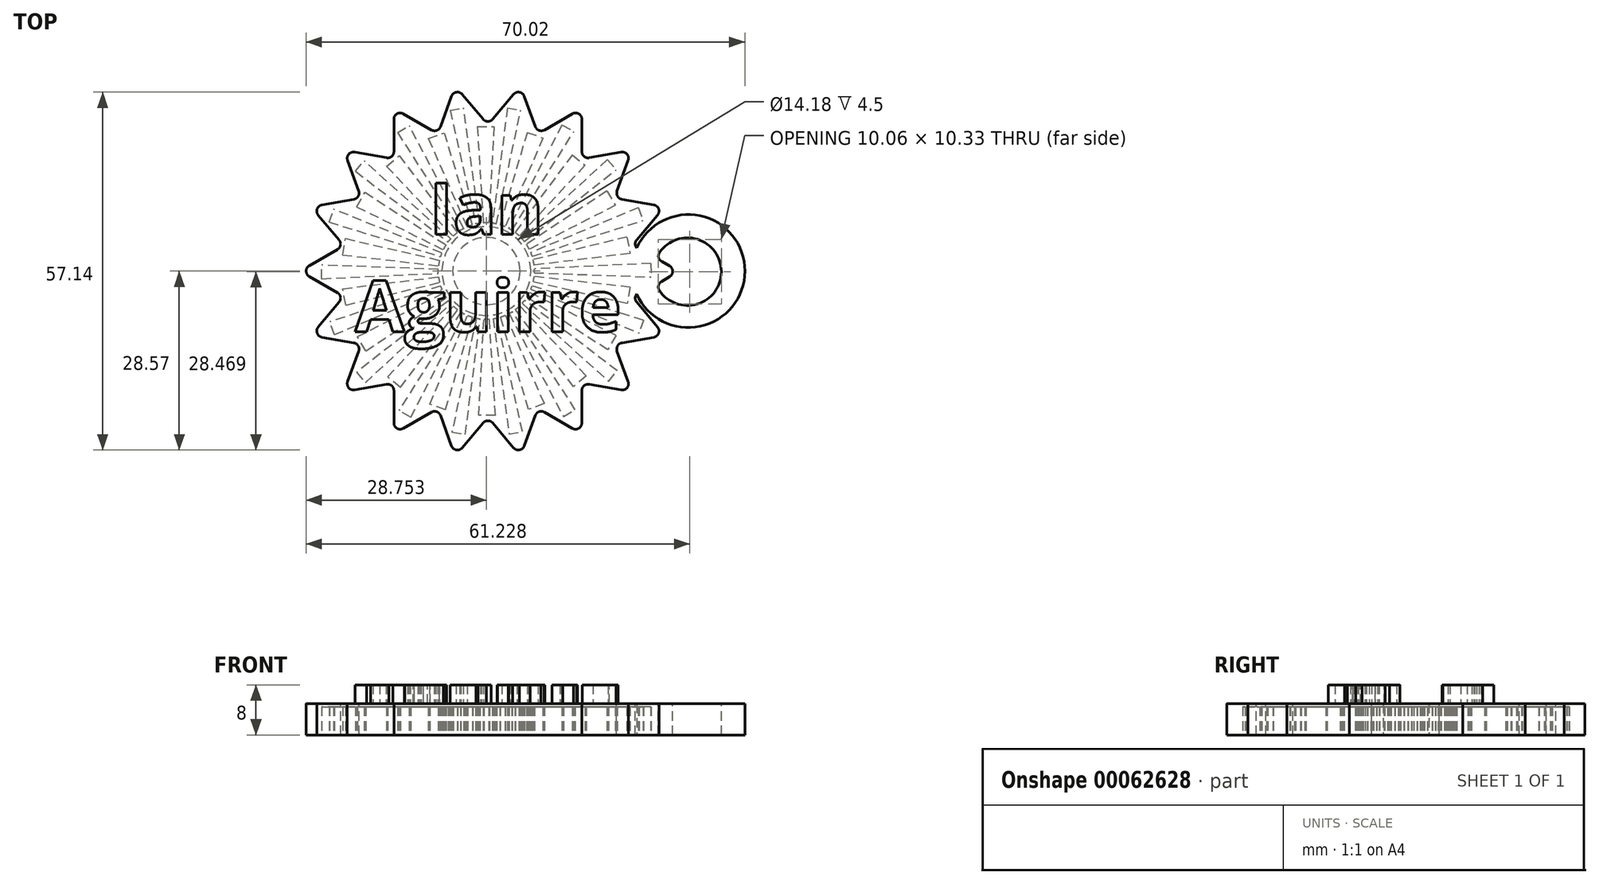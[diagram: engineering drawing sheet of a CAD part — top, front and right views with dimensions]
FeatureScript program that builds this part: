
annotation { "Feature Type Name" : "Feature", "Feature Type Description" : "" }
export const myFeature = defineFeature(function(context is Context, id is Id, definition is map)
    precondition{}
    {
        {
            var Q0;
            Q0=qCreatedBy(makeId("Top.planeOp"),FACE);
            var sketch = newSketch(context, id + "F0", { "sketchPlane" : qUnion([Q0])});
            skLineSegment(sketch, "E0", {"start": v(-64.22, 4.05) * mm, "end": v(-69.43, 10.26) * mm});
            skLineSegment(sketch, "E1", {"start": v(-69.43, 10.26) * mm, "end": v(-61.45, 11.67) * mm});
            skCircle(sketch, "E2.0", {"center": v(-41.24, 0) * mm, "radius": 30 * mm, "construction": true});
            skLineSegment(sketch, "E3", {"start": v(-61.45, 11.67) * mm, "end": v(-64.22, 19.28) * mm});
            skLineSegment(sketch, "E4", {"start": v(-64.22, 19.28) * mm, "end": v(-56.24, 17.88) * mm});
            skLineSegment(sketch, "E5", {"start": v(-56.24, 17.88) * mm, "end": v(-56.24, 25.98) * mm});
            skLineSegment(sketch, "E6", {"start": v(-56.24, 25.98) * mm, "end": v(-49.22, 21.93) * mm});
            skLineSegment(sketch, "E7", {"start": v(-49.22, 21.93) * mm, "end": v(-46.45, 29.54) * mm});
            skLineSegment(sketch, "E8", {"start": v(-46.45, 29.54) * mm, "end": v(-41.24, 23.34) * mm});
            skLineSegment(sketch, "E9", {"start": v(-41.24, 23.34) * mm, "end": v(-36.03, 29.54) * mm});
            skLineSegment(sketch, "E10", {"start": v(-36.03, 29.54) * mm, "end": v(-33.26, 21.93) * mm});
            skLineSegment(sketch, "E11", {"start": v(-33.26, 21.93) * mm, "end": v(-26.24, 25.98) * mm});
            skLineSegment(sketch, "E12", {"start": v(-26.24, 25.98) * mm, "end": v(-26.24, 17.88) * mm});
            skLineSegment(sketch, "E13", {"start": v(-26.24, 17.88) * mm, "end": v(-18.26, 19.28) * mm});
            skLineSegment(sketch, "E14", {"start": v(-18.26, 19.28) * mm, "end": v(-21.03, 11.67) * mm});
            skLineSegment(sketch, "E15", {"start": v(-21.03, 11.67) * mm, "end": v(-13.05, 10.26) * mm});
            skLineSegment(sketch, "E16", {"start": v(-13.05, 10.26) * mm, "end": v(-18.26, 4.05) * mm});
            skLineSegment(sketch, "E17", {"start": v(-18.26, 4.05) * mm, "end": v(-11.24, 0) * mm});
            skLineSegment(sketch, "E18", {"start": v(-11.24, 0) * mm, "end": v(-18.26, -4.05) * mm});
            skLineSegment(sketch, "E19", {"start": v(-18.26, -4.05) * mm, "end": v(-13.05, -10.26) * mm});
            skLineSegment(sketch, "E20", {"start": v(-13.05, -10.26) * mm, "end": v(-21.03, -11.67) * mm});
            skLineSegment(sketch, "E21", {"start": v(-21.03, -11.67) * mm, "end": v(-18.26, -19.28) * mm});
            skLineSegment(sketch, "E22", {"start": v(-18.26, -19.28) * mm, "end": v(-26.24, -17.88) * mm});
            skLineSegment(sketch, "E23", {"start": v(-26.24, -17.88) * mm, "end": v(-26.24, -25.98) * mm});
            skLineSegment(sketch, "E24", {"start": v(-26.24, -25.98) * mm, "end": v(-33.26, -21.93) * mm});
            skLineSegment(sketch, "E25", {"start": v(-33.26, -21.93) * mm, "end": v(-36.03, -29.54) * mm});
            skLineSegment(sketch, "E26", {"start": v(-46.45, -29.54) * mm, "end": v(-49.22, -21.93) * mm});
            skLineSegment(sketch, "E27", {"start": v(-49.22, -21.93) * mm, "end": v(-56.24, -25.98) * mm});
            skLineSegment(sketch, "E28", {"start": v(-56.24, -25.98) * mm, "end": v(-56.24, -17.88) * mm});
            skLineSegment(sketch, "E29", {"start": v(-56.24, -17.88) * mm, "end": v(-64.22, -19.28) * mm});
            skLineSegment(sketch, "E30", {"start": v(-64.22, -19.28) * mm, "end": v(-61.45, -11.67) * mm});
            skLineSegment(sketch, "E31", {"start": v(-61.45, -11.67) * mm, "end": v(-69.43, -10.26) * mm});
            skLineSegment(sketch, "E32", {"start": v(-69.43, -10.26) * mm, "end": v(-64.22, -4.05) * mm});
            skLineSegment(sketch, "E33", {"start": v(-64.22, -4.05) * mm, "end": v(-71.24, 0) * mm});
            skLineSegment(sketch, "E34", {"start": v(-71.24, 0) * mm, "end": v(-64.22, 4.05) * mm});
            skLineSegment(sketch, "E35", {"start": v(-46.45, -29.54) * mm, "end": v(-41.24, -23.34) * mm});
            skLineSegment(sketch, "E36", {"start": v(-41.24, -23.34) * mm, "end": v(-36.03, -29.54) * mm});
            skSolve(sketch);
        }
        {
            var Q0;
            Q0=qSketchRegion(id+"F0",true);
            extrude(context, id + "F1", {"entities" : qUnion([Q0]), "depth" : 5 * mm});
        }
        {
            var Q0;
            Q0=makeQuery(id+"F1.opExtrude","SWEPT_EDGE",EDGE,{"disambiguationData":[OSD([sQuery(id+"F0.wireOp",EDGE,"E26"),sQuery(id+"F0.wireOp",EDGE,"E27")])]});
            var Q1;
            Q1=makeQuery(id+"F1.opExtrude","SWEPT_EDGE",EDGE,{"disambiguationData":[OSD([sQuery(id+"F0.wireOp",EDGE,"E28"),sQuery(id+"F0.wireOp",EDGE,"E29")])]});
            var Q2;
            Q2=makeQuery(id+"F1.opExtrude","SWEPT_EDGE",EDGE,{"disambiguationData":[OSD([sQuery(id+"F0.wireOp",EDGE,"E30"),sQuery(id+"F0.wireOp",EDGE,"E31")])]});
            var Q3;
            Q3=makeQuery(id+"F1.opExtrude","SWEPT_EDGE",EDGE,{"disambiguationData":[OSD([sQuery(id+"F0.wireOp",EDGE,"E32"),sQuery(id+"F0.wireOp",EDGE,"E33")])]});
            var Q4;
            Q4=makeQuery(id+"F1.opExtrude","SWEPT_EDGE",EDGE,{"disambiguationData":[OSD([sQuery(id+"F0.wireOp",EDGE,"E0"),sQuery(id+"F0.wireOp",EDGE,"E34")])]});
            var Q5;
            Q5=makeQuery(id+"F1.opExtrude","SWEPT_EDGE",EDGE,{"disambiguationData":[OSD([sQuery(id+"F0.wireOp",EDGE,"E1"),sQuery(id+"F0.wireOp",EDGE,"E3")])]});
            var Q6;
            Q6=makeQuery(id+"F1.opExtrude","SWEPT_EDGE",EDGE,{"disambiguationData":[OSD([sQuery(id+"F0.wireOp",EDGE,"E4"),sQuery(id+"F0.wireOp",EDGE,"E5")])]});
            var Q7;
            Q7=makeQuery(id+"F1.opExtrude","SWEPT_EDGE",EDGE,{"disambiguationData":[OSD([sQuery(id+"F0.wireOp",EDGE,"E6"),sQuery(id+"F0.wireOp",EDGE,"E7")])]});
            var Q8;
            Q8=makeQuery(id+"F1.opExtrude","SWEPT_EDGE",EDGE,{"disambiguationData":[OSD([sQuery(id+"F0.wireOp",EDGE,"E8"),sQuery(id+"F0.wireOp",EDGE,"E9")])]});
            var Q9;
            Q9=makeQuery(id+"F1.opExtrude","SWEPT_EDGE",EDGE,{"disambiguationData":[OSD([sQuery(id+"F0.wireOp",EDGE,"E10"),sQuery(id+"F0.wireOp",EDGE,"E11")])]});
            var Q10;
            Q10=makeQuery(id+"F1.opExtrude","SWEPT_EDGE",EDGE,{"disambiguationData":[OSD([sQuery(id+"F0.wireOp",EDGE,"E35"),sQuery(id+"F0.wireOp",EDGE,"E36")])]});
            var Q11;
            Q11=makeQuery(id+"F1.opExtrude","SWEPT_EDGE",EDGE,{"disambiguationData":[OSD([sQuery(id+"F0.wireOp",EDGE,"E24"),sQuery(id+"F0.wireOp",EDGE,"E25")])]});
            var Q12;
            Q12=makeQuery(id+"F1.opExtrude","SWEPT_EDGE",EDGE,{"disambiguationData":[OSD([sQuery(id+"F0.wireOp",EDGE,"E22"),sQuery(id+"F0.wireOp",EDGE,"E23")])]});
            var Q13;
            Q13=makeQuery(id+"F1.opExtrude","SWEPT_EDGE",EDGE,{"disambiguationData":[OSD([sQuery(id+"F0.wireOp",EDGE,"E20"),sQuery(id+"F0.wireOp",EDGE,"E21")])]});
            var Q14;
            Q14=makeQuery(id+"F1.opExtrude","SWEPT_EDGE",EDGE,{"disambiguationData":[OSD([sQuery(id+"F0.wireOp",EDGE,"E12"),sQuery(id+"F0.wireOp",EDGE,"E13")])]});
            var Q15;
            Q15=makeQuery(id+"F1.opExtrude","SWEPT_EDGE",EDGE,{"disambiguationData":[OSD([sQuery(id+"F0.wireOp",EDGE,"E14"),sQuery(id+"F0.wireOp",EDGE,"E15")])]});
            var Q16;
            Q16=makeQuery(id+"F1.opExtrude","SWEPT_EDGE",EDGE,{"disambiguationData":[OSD([sQuery(id+"F0.wireOp",EDGE,"E16"),sQuery(id+"F0.wireOp",EDGE,"E17")])]});
            var Q17;
            Q17=makeQuery(id+"F1.opExtrude","SWEPT_EDGE",EDGE,{"disambiguationData":[OSD([sQuery(id+"F0.wireOp",EDGE,"E18"),sQuery(id+"F0.wireOp",EDGE,"E19")])]});
            fillet(context, id + "F2", {"entities" : qUnion([Q0, Q1, Q2, Q3, Q4, Q5, Q6, Q7, Q8, Q9, Q10, Q11, Q12, Q13, Q14, Q15, Q16, Q17]), "radius" : 1 * mm, "tangentPropagation" : true, "allowEdgeOverflow" : false});
        }
        {
            var Q0;
            Q0=makeQuery(id+"F1.opExtrude","SWEPT_EDGE",EDGE,{"disambiguationData":[OSD([sQuery(id+"F0.wireOp",EDGE,"E9"),sQuery(id+"F0.wireOp",EDGE,"E10")])]});
            var Q1;
            Q1=makeQuery(id+"F1.opExtrude","SWEPT_EDGE",EDGE,{"disambiguationData":[OSD([sQuery(id+"F0.wireOp",EDGE,"E11"),sQuery(id+"F0.wireOp",EDGE,"E12")])]});
            var Q2;
            Q2=makeQuery(id+"F1.opExtrude","SWEPT_EDGE",EDGE,{"disambiguationData":[OSD([sQuery(id+"F0.wireOp",EDGE,"E13"),sQuery(id+"F0.wireOp",EDGE,"E14")])]});
            var Q3;
            Q3=makeQuery(id+"F1.opExtrude","SWEPT_EDGE",EDGE,{"disambiguationData":[OSD([sQuery(id+"F0.wireOp",EDGE,"E15"),sQuery(id+"F0.wireOp",EDGE,"E16")])]});
            var Q4;
            Q4=makeQuery(id+"F1.opExtrude","SWEPT_EDGE",EDGE,{"disambiguationData":[OSD([sQuery(id+"F0.wireOp",EDGE,"E17"),sQuery(id+"F0.wireOp",EDGE,"E18")])]});
            var Q5;
            Q5=makeQuery(id+"F1.opExtrude","SWEPT_EDGE",EDGE,{"disambiguationData":[OSD([sQuery(id+"F0.wireOp",EDGE,"E19"),sQuery(id+"F0.wireOp",EDGE,"E20")])]});
            var Q6;
            Q6=makeQuery(id+"F1.opExtrude","SWEPT_EDGE",EDGE,{"disambiguationData":[OSD([sQuery(id+"F0.wireOp",EDGE,"E5"),sQuery(id+"F0.wireOp",EDGE,"E6")])]});
            var Q7;
            Q7=makeQuery(id+"F1.opExtrude","SWEPT_EDGE",EDGE,{"disambiguationData":[OSD([sQuery(id+"F0.wireOp",EDGE,"E7"),sQuery(id+"F0.wireOp",EDGE,"E8")])]});
            var Q8;
            Q8=makeQuery(id+"F1.opExtrude","SWEPT_EDGE",EDGE,{"disambiguationData":[OSD([sQuery(id+"F0.wireOp",EDGE,"E3"),sQuery(id+"F0.wireOp",EDGE,"E4")])]});
            var Q9;
            Q9=makeQuery(id+"F1.opExtrude","SWEPT_EDGE",EDGE,{"disambiguationData":[OSD([sQuery(id+"F0.wireOp",EDGE,"E0"),sQuery(id+"F0.wireOp",EDGE,"E1")])]});
            var Q10;
            Q10=makeQuery(id+"F1.opExtrude","SWEPT_EDGE",EDGE,{"disambiguationData":[OSD([sQuery(id+"F0.wireOp",EDGE,"E33"),sQuery(id+"F0.wireOp",EDGE,"E34")])]});
            var Q11;
            Q11=makeQuery(id+"F1.opExtrude","SWEPT_EDGE",EDGE,{"disambiguationData":[OSD([sQuery(id+"F0.wireOp",EDGE,"E31"),sQuery(id+"F0.wireOp",EDGE,"E32")])]});
            var Q12;
            Q12=makeQuery(id+"F1.opExtrude","SWEPT_EDGE",EDGE,{"disambiguationData":[OSD([sQuery(id+"F0.wireOp",EDGE,"E29"),sQuery(id+"F0.wireOp",EDGE,"E30")])]});
            var Q13;
            Q13=makeQuery(id+"F1.opExtrude","SWEPT_EDGE",EDGE,{"disambiguationData":[OSD([sQuery(id+"F0.wireOp",EDGE,"E27"),sQuery(id+"F0.wireOp",EDGE,"E28")])]});
            var Q14;
            Q14=makeQuery(id+"F1.opExtrude","SWEPT_EDGE",EDGE,{"disambiguationData":[OSD([sQuery(id+"F0.wireOp",EDGE,"E26"),sQuery(id+"F0.wireOp",EDGE,"E35")])]});
            var Q15;
            Q15=makeQuery(id+"F1.opExtrude","SWEPT_EDGE",EDGE,{"disambiguationData":[OSD([sQuery(id+"F0.wireOp",EDGE,"E25"),sQuery(id+"F0.wireOp",EDGE,"E36")])]});
            var Q16;
            Q16=makeQuery(id+"F1.opExtrude","SWEPT_EDGE",EDGE,{"disambiguationData":[OSD([sQuery(id+"F0.wireOp",EDGE,"E23"),sQuery(id+"F0.wireOp",EDGE,"E24")])]});
            var Q17;
            Q17=makeQuery(id+"F1.opExtrude","SWEPT_EDGE",EDGE,{"disambiguationData":[OSD([sQuery(id+"F0.wireOp",EDGE,"E21"),sQuery(id+"F0.wireOp",EDGE,"E22")])]});
            fillet(context, id + "F3", {"entities" : qUnion([Q0, Q1, Q2, Q3, Q4, Q5, Q6, Q7, Q8, Q9, Q10, Q11, Q12, Q13, Q14, Q15, Q16, Q17]), "radius" : 1 * mm, "tangentPropagation" : true, "allowEdgeOverflow" : false});
        }
        {
            var Q0;
            Q0=qCreatedBy(makeId("Top.planeOp"),FACE);
            var sketch = newSketch(context, id + "F4", { "sketchPlane" : qUnion([Q0])});
            skCircle(sketch, "E37", {"center": v(-9.24, 0) * mm, "radius": 9.02 * mm});
            skSolve(sketch);
        }
        {
            var Q0;
            Q0=qSketchRegion(id+"F4",true);
            var Q1;
            {var subQ0=sQuery(id+"F0.wireOp",EDGE,"E30");var subQ1=sQuery(id+"F0.wireOp",EDGE,"E16");var subQ2=sQuery(id+"F0.wireOp",EDGE,"E31");var subQ3=sQuery(id+"F0.wireOp",EDGE,"E27");var subQ4=sQuery(id+"F0.wireOp",EDGE,"E23");var subQ5=sQuery(id+"F0.wireOp",EDGE,"E21");var subQ6=sQuery(id+"F0.wireOp",EDGE,"E13");var subQ7=sQuery(id+"F0.wireOp",EDGE,"E14");var subQ8=sQuery(id+"F0.wireOp",EDGE,"E20");var subQ9=sQuery(id+"F0.wireOp",EDGE,"E22");var subQ10=sQuery(id+"F0.wireOp",EDGE,"E19");var subQ11=sQuery(id+"F0.wireOp",EDGE,"E11");var subQ12=sQuery(id+"F0.wireOp",EDGE,"E18");var subQ13=sQuery(id+"F0.wireOp",EDGE,"E17");var subQ14=sQuery(id+"F0.wireOp",EDGE,"E12");var subQ15=sQuery(id+"F0.wireOp",EDGE,"E4");var subQ16=sQuery(id+"F0.wireOp",EDGE,"E3");var subQ17=sQuery(id+"F0.wireOp",EDGE,"E32");var subQ18=sQuery(id+"F0.wireOp",EDGE,"E1");var subQ19=sQuery(id+"F0.wireOp",EDGE,"E9");var subQ20=sQuery(id+"F0.wireOp",EDGE,"E0");var subQ21=sQuery(id+"F0.wireOp",EDGE,"E5");var subQ22=sQuery(id+"F0.wireOp",EDGE,"E6");var subQ23=sQuery(id+"F0.wireOp",EDGE,"E7");var subQ24=sQuery(id+"F0.wireOp",EDGE,"E36");var subQ25=sQuery(id+"F0.wireOp",EDGE,"E15");var subQ26=sQuery(id+"F0.wireOp",EDGE,"E8");var subQ27=sQuery(id+"F0.wireOp",EDGE,"E34");var subQ28=sQuery(id+"F0.wireOp",EDGE,"E25");var subQ29=sQuery(id+"F0.wireOp",EDGE,"E29");var subQ30=sQuery(id+"F0.wireOp",EDGE,"E26");var subQ31=sQuery(id+"F0.wireOp",EDGE,"E35");var subQ32=sQuery(id+"F0.wireOp",EDGE,"E33");var subQ33=sQuery(id+"F0.wireOp",EDGE,"E24");var subQ34=sQuery(id+"F0.wireOp",EDGE,"E10");var subQ35=sQuery(id+"F0.wireOp",EDGE,"E28");Q1=makeQuery(id+"FIdaEZY0NoQjCEp_1.boolean.opBoolean","SPLIT",FACE,{"disambiguationData":[TD([makeQuery(id+"F1.opExtrude","SWEPT_FACE",FACE,{"disambiguationData":[OSD([subQ20])]})])],"derivedFrom":makeQuery(id+"F1.opExtrude","CAP_FACE",FACE,{"disambiguationData":[OSD([subQ20,subQ18,subQ16,subQ15,subQ21,subQ22,subQ23,subQ26,subQ19,subQ34,subQ11,subQ14,subQ6,subQ7,subQ25,subQ1,subQ13,subQ12,subQ10,subQ8,subQ5,subQ9,subQ4,subQ33,subQ28,subQ30,subQ3,subQ35,subQ29,subQ0,subQ2,subQ17,subQ32,subQ27,subQ31,subQ24])],"isStart":false})});}
            extrude(context, id + "F5", {"entities" : qUnion([Q0]), "operationType" : NewBodyOperationType.ADD, "endBound" : BoundingType.UP_TO_SURFACE, "endBoundEntityFace" : qUnion([Q1]), "depth" : 25 * mm});
        }
        {
            var Q0;
            {var subQ0=sQuery(id+"F0.wireOp",EDGE,"E36");var subQ1=sQuery(id+"F0.wireOp",EDGE,"E35");var subQ2=sQuery(id+"F0.wireOp",EDGE,"E34");var subQ3=sQuery(id+"F0.wireOp",EDGE,"E33");var subQ4=sQuery(id+"F0.wireOp",EDGE,"E32");var subQ5=sQuery(id+"F0.wireOp",EDGE,"E31");var subQ6=sQuery(id+"F0.wireOp",EDGE,"E30");var subQ7=sQuery(id+"F0.wireOp",EDGE,"E29");var subQ8=sQuery(id+"F0.wireOp",EDGE,"E28");var subQ9=sQuery(id+"F0.wireOp",EDGE,"E27");var subQ10=sQuery(id+"F0.wireOp",EDGE,"E26");var subQ11=sQuery(id+"F0.wireOp",EDGE,"E25");var subQ12=sQuery(id+"F0.wireOp",EDGE,"E24");var subQ13=sQuery(id+"F0.wireOp",EDGE,"E23");var subQ14=sQuery(id+"F0.wireOp",EDGE,"E22");var subQ15=sQuery(id+"F0.wireOp",EDGE,"E21");var subQ16=sQuery(id+"F0.wireOp",EDGE,"E20");var subQ17=sQuery(id+"F0.wireOp",EDGE,"E19");var subQ18=sQuery(id+"F0.wireOp",EDGE,"E18");var subQ19=sQuery(id+"F0.wireOp",EDGE,"E17");var subQ20=sQuery(id+"F0.wireOp",EDGE,"E16");var subQ21=sQuery(id+"F0.wireOp",EDGE,"E15");var subQ22=sQuery(id+"F0.wireOp",EDGE,"E14");var subQ23=sQuery(id+"F0.wireOp",EDGE,"E13");var subQ24=sQuery(id+"F0.wireOp",EDGE,"E12");var subQ25=sQuery(id+"F0.wireOp",EDGE,"E11");var subQ26=sQuery(id+"F0.wireOp",EDGE,"E10");var subQ27=sQuery(id+"F0.wireOp",EDGE,"E9");var subQ28=sQuery(id+"F0.wireOp",EDGE,"E8");var subQ29=sQuery(id+"F0.wireOp",EDGE,"E7");var subQ30=sQuery(id+"F0.wireOp",EDGE,"E6");var subQ31=sQuery(id+"F0.wireOp",EDGE,"E5");var subQ32=sQuery(id+"F0.wireOp",EDGE,"E4");var subQ33=sQuery(id+"F0.wireOp",EDGE,"E3");var subQ34=sQuery(id+"F0.wireOp",EDGE,"E1");var subQ35=sQuery(id+"F0.wireOp",EDGE,"E0");Q0=makeQuery(id+"F5.boolean.opBoolean","MERGE",FACE,{"derivedFrom":[makeQuery(id+"F1.opExtrude","CAP_FACE",FACE,{"disambiguationData":[OSD([subQ35,subQ34,subQ33,subQ32,subQ31,subQ30,subQ29,subQ28,subQ27,subQ26,subQ25,subQ24,subQ23,subQ22,subQ21,subQ20,subQ19,subQ18,subQ17,subQ16,subQ15,subQ14,subQ13,subQ12,subQ11,subQ10,subQ9,subQ8,subQ7,subQ6,subQ5,subQ4,subQ3,subQ2,subQ1,subQ0])],"isStart":false}),makeQuery(id+"F5.opExtrude","CAP_FACE",FACE,{"disambiguationData":[OSD([subQ35,subQ34,subQ33,subQ32,subQ31,subQ30,subQ29,subQ28,subQ27,subQ26,subQ25,subQ24,subQ23,subQ22,subQ21,subQ20,subQ19,subQ18,subQ17,subQ16,subQ15,subQ14,subQ13,subQ12,subQ11,subQ10,subQ9,subQ8,subQ7,subQ6,subQ5,subQ4,subQ3,subQ2,subQ1,subQ0])],"isStart":false})]});}
            var sketch = newSketch(context, id + "F6", { "sketchPlane" : qUnion([Q0])});
            skLineSegment(sketch, "E38", {"start": v(-14.37, 2) * mm, "end": v(-10.75, 0) * mm});
            skLineSegment(sketch, "E39", {"start": v(-10.75, 0) * mm, "end": v(-14.37, -2.19) * mm});
            skArc(sketch, "E40", {"start": v(-14.37, -2.19) * mm, "mid": v(-3.98, -0.1) * mm, "end": v(-14.37, 2) * mm});
            skSolve(sketch);
        }
        {
            var Q0;
            Q0=qSketchRegion(id+"F6",true);
            var Q1;
            Q1=makeQuery(id+"F5.boolean.opBoolean","MERGE",FACE,{"derivedFrom":[makeQuery(id+"F1.opExtrude","CAP_FACE",FACE,{"disambiguationData":[OSD([sQuery(id+"F0.wireOp",EDGE,"E0"),sQuery(id+"F0.wireOp",EDGE,"E1"),sQuery(id+"F0.wireOp",EDGE,"E3"),sQuery(id+"F0.wireOp",EDGE,"E4"),sQuery(id+"F0.wireOp",EDGE,"E5"),sQuery(id+"F0.wireOp",EDGE,"E6"),sQuery(id+"F0.wireOp",EDGE,"E7"),sQuery(id+"F0.wireOp",EDGE,"E8"),sQuery(id+"F0.wireOp",EDGE,"E9"),sQuery(id+"F0.wireOp",EDGE,"E10"),sQuery(id+"F0.wireOp",EDGE,"E11"),sQuery(id+"F0.wireOp",EDGE,"E12"),sQuery(id+"F0.wireOp",EDGE,"E13"),sQuery(id+"F0.wireOp",EDGE,"E14"),sQuery(id+"F0.wireOp",EDGE,"E15"),sQuery(id+"F0.wireOp",EDGE,"E16"),sQuery(id+"F0.wireOp",EDGE,"E17"),sQuery(id+"F0.wireOp",EDGE,"E18"),sQuery(id+"F0.wireOp",EDGE,"E19"),sQuery(id+"F0.wireOp",EDGE,"E20"),sQuery(id+"F0.wireOp",EDGE,"E21"),sQuery(id+"F0.wireOp",EDGE,"E22"),sQuery(id+"F0.wireOp",EDGE,"E23"),sQuery(id+"F0.wireOp",EDGE,"E24"),sQuery(id+"F0.wireOp",EDGE,"E25"),sQuery(id+"F0.wireOp",EDGE,"E26"),sQuery(id+"F0.wireOp",EDGE,"E27"),sQuery(id+"F0.wireOp",EDGE,"E28"),sQuery(id+"F0.wireOp",EDGE,"E29"),sQuery(id+"F0.wireOp",EDGE,"E30"),sQuery(id+"F0.wireOp",EDGE,"E31"),sQuery(id+"F0.wireOp",EDGE,"E32"),sQuery(id+"F0.wireOp",EDGE,"E33"),sQuery(id+"F0.wireOp",EDGE,"E34"),sQuery(id+"F0.wireOp",EDGE,"E35"),sQuery(id+"F0.wireOp",EDGE,"E36")])],"isStart":true}),makeQuery(id+"F5.opExtrude","CAP_FACE",FACE,{"disambiguationData":[OSD([sQuery(id+"F4.wireOp",EDGE,"E37")])],"isStart":true})]});
            extrude(context, id + "F7", {"entities" : qUnion([Q0]), "operationType" : NewBodyOperationType.REMOVE, "endBound" : BoundingType.UP_TO_SURFACE, "oppositeDirection" : true, "endBoundEntityFace" : qUnion([Q1]), "depth" : 25 * mm});
        }
        {
            var Q0;
            Q0=makeQuery(id+"F7.boolean.opBoolean","COPY",EDGE,{"derivedFrom":makeQuery(id+"F7.opExtrude","SWEPT_EDGE",EDGE,{"disambiguationData":[OSD([sQuery(id+"F6.wireOp",EDGE,"KMGjyx1H-Efwy-Ger7-KHIj-FZDtgPy88TKw"),sQuery(id+"F6.wireOp",EDGE,"Em1Z4o3I-NRpS-VtHU-MFej-VVcVSapDzxZl")])]})});
            var Q1;
            Q1=makeQuery(id+"F7.boolean.opBoolean","COPY",EDGE,{"derivedFrom":makeQuery(id+"F7.opExtrude","SWEPT_EDGE",EDGE,{"disambiguationData":[OSD([sQuery(id+"F6.wireOp",EDGE,"E38"),sQuery(id+"F6.wireOp",EDGE,"E39")])]})});
            var Q2;
            Q2=makeQuery(id+"F7.boolean.opBoolean","COPY",EDGE,{"derivedFrom":makeQuery(id+"F7.opExtrude","SWEPT_EDGE",EDGE,{"disambiguationData":[OSD([sQuery(id+"F6.wireOp",EDGE,"E39"),sQuery(id+"F6.wireOp",EDGE,"E40")])]})});
            var Q3;
            Q3=makeQuery(id+"F7.boolean.opBoolean","COPY",EDGE,{"derivedFrom":makeQuery(id+"F7.opExtrude","SWEPT_EDGE",EDGE,{"disambiguationData":[OSD([sQuery(id+"F6.wireOp",EDGE,"E38"),sQuery(id+"F6.wireOp",EDGE,"E40")])]})});
            fillet(context, id + "F8", {"entities" : qUnion([Q0, Q1, Q2, Q3]), "radius" : 1 * mm, "tangentPropagation" : true, "allowEdgeOverflow" : false});
        }
        {
            var Q0;
            Q0=makeQuery(id+"F0.imprint","IMPRINT",FACE,{"disambiguationData":[TD([[makeQuery(id+"F0.imprint","IMPRINT",EDGE,{"derivedFrom":sQuery(id+"F0.wireOp",EDGE,"E0")}),-1.0]])]});
            var sketch = newSketch(context, id + "F9", { "sketchPlane" : qUnion([Q0])});
            skCircle(sketch, "E41", {"center": v(-41.49, 0) * mm, "radius": 26.28 * mm, "construction": true});
            skCircle(sketch, "E42", {"center": v(-41.49, 0) * mm, "radius": 23.08 * mm, "construction": true});
            skLineSegment(sketch, "E43", {"start": v(-41.49, 0) * mm, "end": v(-21.98, -17.6) * mm, "construction": true});
            skLineSegment(sketch, "E44", {"start": v(-21.98, -17.6) * mm, "end": v(-20.6, -15.94) * mm, "construction": true});
            skLineSegment(sketch, "E45", {"start": v(-20.6, -15.94) * mm, "end": v(-41.49, 0) * mm, "construction": true});
            skLineSegment(sketch, "E46", {"start": v(-41.49, 0) * mm, "end": v(-22.13, -12.57) * mm, "construction": true});
            skLineSegment(sketch, "E47", {"start": v(-22.13, -12.57) * mm, "end": v(-20.8, -10.26) * mm, "construction": true});
            skLineSegment(sketch, "E48", {"start": v(-20.8, -10.26) * mm, "end": v(-41.49, 0) * mm, "construction": true});
            skLineSegment(sketch, "E49", {"start": v(-41.49, 0) * mm, "end": v(-21.03, -11.67) * mm, "construction": true});
            skLineSegment(sketch, "E50", {"start": v(-41.49, 0) * mm, "end": v(-18.26, -19.28) * mm, "construction": true});
            skLineSegment(sketch, "E51", {"start": v(-20.8, -10.26) * mm, "end": v(-21.03, -11.67) * mm, "construction": true});
            skLineSegment(sketch, "E52", {"start": v(-22.13, -12.57) * mm, "end": v(-21.03, -11.67) * mm, "construction": true});
            skLineSegment(sketch, "E53", {"start": v(-18.26, -19.28) * mm, "end": v(-21.98, -17.6) * mm, "construction": true});
            skLineSegment(sketch, "E54", {"start": v(-20.6, -15.94) * mm, "end": v(-18.26, -19.28) * mm, "construction": true});
            skLineSegment(sketch, "E55", {"start": v(-35.78, -5.15) * mm, "end": v(-21.98, -17.6) * mm});
            skLineSegment(sketch, "E56", {"start": v(-20.6, -15.94) * mm, "end": v(-35.38, -4.66) * mm});
            skLineSegment(sketch, "E57", {"start": v(-22.13, -12.57) * mm, "end": v(-35.04, -4.18) * mm});
            skLineSegment(sketch, "E58", {"start": v(-20.8, -10.26) * mm, "end": v(-22.13, -12.57) * mm});
            skLineSegment(sketch, "E59", {"start": v(-20.8, -10.26) * mm, "end": v(-34.6, -3.42) * mm});
            skLineSegment(sketch, "E60.1.0", {"start": v(-34.37, -2.89) * mm, "end": v(-17.13, -9.87) * mm});
            skLineSegment(sketch, "E60.1.1", {"start": v(-17.13, -9.87) * mm, "end": v(-16.4, -7.83) * mm, "construction": true});
            skLineSegment(sketch, "E60.1.2", {"start": v(-16.4, -7.83) * mm, "end": v(-19.45, -6.88) * mm});
            skLineSegment(sketch, "E60.1.3", {"start": v(-19, -5.2) * mm, "end": v(-34, -1.73) * mm});
            skLineSegment(sketch, "E60.1.4", {"start": v(-18.55, -2.57) * mm, "end": v(-19, -5.2) * mm});
            skLineSegment(sketch, "E60.1.5", {"start": v(-18.55, -2.57) * mm, "end": v(-33.85, -0.86) * mm});
            skLineSegment(sketch, "E60.2.0", {"start": v(-33.8, -0.28) * mm, "end": v(-15.22, -0.95) * mm});
            skLineSegment(sketch, "E60.2.1", {"start": v(-15.22, -0.95) * mm, "end": v(-15.23, 1.22) * mm, "construction": true});
            skLineSegment(sketch, "E60.2.2", {"start": v(-15.23, 1.22) * mm, "end": v(-33.81, 0.36) * mm});
            skLineSegment(sketch, "E60.2.3", {"start": v(-18.57, 2.81) * mm, "end": v(-33.86, 0.94) * mm});
            skLineSegment(sketch, "E60.2.4", {"start": v(-19.05, 5.43) * mm, "end": v(-18.57, 2.81) * mm});
            skLineSegment(sketch, "E60.2.5", {"start": v(-19.05, 5.43) * mm, "end": v(-34.02, 1.8) * mm});
            skLineSegment(sketch, "E60.3.0", {"start": v(-34.18, 2.37) * mm, "end": v(-16.48, 8.1) * mm});
            skLineSegment(sketch, "E60.3.1", {"start": v(-16.48, 8.1) * mm, "end": v(-17.23, 10.13) * mm, "construction": true});
            skLineSegment(sketch, "E60.3.2", {"start": v(-17.23, 10.13) * mm, "end": v(-34.4, 2.96) * mm});
            skLineSegment(sketch, "E60.3.3", {"start": v(-20.92, 10.48) * mm, "end": v(-34.64, 3.49) * mm});
            skLineSegment(sketch, "E60.3.4", {"start": v(-22.26, 12.78) * mm, "end": v(-20.92, 10.48) * mm});
            skLineSegment(sketch, "E60.3.5", {"start": v(-22.26, 12.78) * mm, "end": v(-35.09, 4.25) * mm});
            skLineSegment(sketch, "E60.4.0", {"start": v(-35.43, 4.72) * mm, "end": v(-20.76, 16.16) * mm});
            skLineSegment(sketch, "E60.4.1", {"start": v(-20.76, 16.16) * mm, "end": v(-22.16, 17.81) * mm, "construction": true});
            skLineSegment(sketch, "E60.4.2", {"start": v(-22.16, 17.81) * mm, "end": v(-35.84, 5.2) * mm});
            skLineSegment(sketch, "E60.4.3", {"start": v(-25.74, 16.88) * mm, "end": v(-36.25, 5.62) * mm});
            skLineSegment(sketch, "E60.4.4", {"start": v(-27.79, 18.58) * mm, "end": v(-25.74, 16.88) * mm});
            skLineSegment(sketch, "E60.4.5", {"start": v(-27.79, 18.58) * mm, "end": v(-36.93, 6.18) * mm});
            skLineSegment(sketch, "E60.5.0", {"start": v(-37.4, 6.51) * mm, "end": v(-27.53, 22.27) * mm});
            skLineSegment(sketch, "E60.5.1", {"start": v(-27.53, 22.27) * mm, "end": v(-29.42, 23.35) * mm, "construction": true});
            skLineSegment(sketch, "E60.5.2", {"start": v(-29.42, 23.35) * mm, "end": v(-37.96, 6.83) * mm});
            skLineSegment(sketch, "E60.5.3", {"start": v(-32.47, 21.25) * mm, "end": v(-38.48, 7.07) * mm});
            skLineSegment(sketch, "E60.5.4", {"start": v(-34.97, 22.15) * mm, "end": v(-32.47, 21.25) * mm});
            skLineSegment(sketch, "E60.5.5", {"start": v(-34.97, 22.15) * mm, "end": v(-39.32, 7.37) * mm});
            skLineSegment(sketch, "E60.6.0", {"start": v(-39.88, 7.51) * mm, "end": v(-36, 25.7) * mm});
            skLineSegment(sketch, "E60.6.1", {"start": v(-36, 25.7) * mm, "end": v(-38.13, 26.07) * mm, "construction": true});
            skLineSegment(sketch, "E60.6.2", {"start": v(-38.13, 26.07) * mm, "end": v(-40.5, 7.62) * mm});
            skLineSegment(sketch, "E60.6.3", {"start": v(-40.28, 23.05) * mm, "end": v(-41.08, 7.67) * mm});
            skLineSegment(sketch, "E60.6.4", {"start": v(-42.94, 23.04) * mm, "end": v(-40.28, 23.05) * mm});
            skLineSegment(sketch, "E60.6.5", {"start": v(-42.94, 23.04) * mm, "end": v(-41.97, 7.67) * mm});
            skLineSegment(sketch, "E60.7.0", {"start": v(-42.55, 7.6) * mm, "end": v(-45.11, 26.03) * mm});
            skLineSegment(sketch, "E60.7.1", {"start": v(-45.11, 26.03) * mm, "end": v(-47.25, 25.64) * mm, "construction": true});
            skLineSegment(sketch, "E60.7.2", {"start": v(-47.25, 25.64) * mm, "end": v(-43.17, 7.5) * mm});
            skLineSegment(sketch, "E60.7.3", {"start": v(-48.24, 22.08) * mm, "end": v(-43.73, 7.35) * mm});
            skLineSegment(sketch, "E60.7.4", {"start": v(-50.73, 21.15) * mm, "end": v(-48.24, 22.08) * mm});
            skLineSegment(sketch, "E60.7.5", {"start": v(-50.73, 21.15) * mm, "end": v(-44.56, 7.04) * mm});
            skLineSegment(sketch, "E60.8.0", {"start": v(-45.09, 6.79) * mm, "end": v(-53.8, 23.22) * mm});
            skLineSegment(sketch, "E60.8.1", {"start": v(-53.8, 23.22) * mm, "end": v(-55.67, 22.13) * mm, "construction": true});
            skLineSegment(sketch, "E60.8.2", {"start": v(-55.67, 22.13) * mm, "end": v(-45.63, 6.47) * mm});
            skLineSegment(sketch, "E60.8.3", {"start": v(-55.38, 18.44) * mm, "end": v(-46.11, 6.14) * mm});
            skLineSegment(sketch, "E60.8.4", {"start": v(-57.4, 16.72) * mm, "end": v(-55.38, 18.44) * mm});
            skLineSegment(sketch, "E60.8.5", {"start": v(-57.4, 16.72) * mm, "end": v(-46.79, 5.56) * mm});
            skLineSegment(sketch, "E60.9.0", {"start": v(-47.2, 5.15) * mm, "end": v(-61, 17.6) * mm});
            skLineSegment(sketch, "E60.9.1", {"start": v(-61, 17.6) * mm, "end": v(-62.38, 15.94) * mm, "construction": true});
            skLineSegment(sketch, "E60.9.2", {"start": v(-62.38, 15.94) * mm, "end": v(-47.6, 4.66) * mm});
            skLineSegment(sketch, "E60.9.3", {"start": v(-60.85, 12.57) * mm, "end": v(-47.93, 4.18) * mm});
            skLineSegment(sketch, "E60.9.4", {"start": v(-62.16, 10.26) * mm, "end": v(-60.85, 12.57) * mm});
            skLineSegment(sketch, "E60.9.5", {"start": v(-62.16, 10.26) * mm, "end": v(-48.37, 3.42) * mm});
            skLineSegment(sketch, "E60.10.0", {"start": v(-48.6, 2.89) * mm, "end": v(-65.84, 9.87) * mm});
            skLineSegment(sketch, "E60.10.1", {"start": v(-65.84, 9.87) * mm, "end": v(-66.57, 7.83) * mm, "construction": true});
            skLineSegment(sketch, "E60.10.2", {"start": v(-66.57, 7.83) * mm, "end": v(-48.82, 2.29) * mm});
            skLineSegment(sketch, "E60.10.3", {"start": v(-63.98, 5.2) * mm, "end": v(-48.97, 1.73) * mm});
            skLineSegment(sketch, "E60.10.4", {"start": v(-64.43, 2.57) * mm, "end": v(-63.98, 5.2) * mm});
            skLineSegment(sketch, "E60.10.5", {"start": v(-64.43, 2.57) * mm, "end": v(-49.12, 0.86) * mm});
            skLineSegment(sketch, "E60.11.0", {"start": v(-49.17, 0.28) * mm, "end": v(-67.75, 0.95) * mm});
            skLineSegment(sketch, "E60.11.1", {"start": v(-67.75, 0.95) * mm, "end": v(-67.74, -1.22) * mm, "construction": true});
            skLineSegment(sketch, "E60.11.2", {"start": v(-67.74, -1.22) * mm, "end": v(-49.16, -0.36) * mm});
            skLineSegment(sketch, "E60.11.3", {"start": v(-64.4, -2.81) * mm, "end": v(-49.11, -0.94) * mm});
            skLineSegment(sketch, "E60.11.4", {"start": v(-63.92, -5.43) * mm, "end": v(-64.4, -2.81) * mm});
            skLineSegment(sketch, "E60.11.5", {"start": v(-63.92, -5.43) * mm, "end": v(-48.95, -1.8) * mm});
            skLineSegment(sketch, "E60.12.0", {"start": v(-48.8, -2.37) * mm, "end": v(-66.5, -8.1) * mm});
            skLineSegment(sketch, "E60.12.1", {"start": v(-66.5, -8.1) * mm, "end": v(-65.74, -10.13) * mm, "construction": true});
            skLineSegment(sketch, "E60.12.2", {"start": v(-65.74, -10.13) * mm, "end": v(-48.58, -2.96) * mm});
            skLineSegment(sketch, "E60.12.3", {"start": v(-62.06, -10.48) * mm, "end": v(-48.33, -3.49) * mm});
            skLineSegment(sketch, "E60.12.4", {"start": v(-60.71, -12.78) * mm, "end": v(-62.06, -10.48) * mm});
            skLineSegment(sketch, "E60.12.5", {"start": v(-60.71, -12.78) * mm, "end": v(-47.89, -4.25) * mm});
            skLineSegment(sketch, "E60.13.0", {"start": v(-47.55, -4.72) * mm, "end": v(-62.22, -16.16) * mm});
            skLineSegment(sketch, "E60.13.1", {"start": v(-62.22, -16.16) * mm, "end": v(-60.81, -17.81) * mm, "construction": true});
            skLineSegment(sketch, "E60.13.2", {"start": v(-60.81, -17.81) * mm, "end": v(-47.14, -5.2) * mm});
            skLineSegment(sketch, "E60.13.3", {"start": v(-57.23, -16.88) * mm, "end": v(-46.73, -5.62) * mm});
            skLineSegment(sketch, "E60.13.4", {"start": v(-55.18, -18.58) * mm, "end": v(-57.23, -16.88) * mm});
            skLineSegment(sketch, "E60.13.5", {"start": v(-55.18, -18.58) * mm, "end": v(-46.05, -6.18) * mm});
            skLineSegment(sketch, "E60.14.0", {"start": v(-45.57, -6.51) * mm, "end": v(-55.44, -22.27) * mm});
            skLineSegment(sketch, "E60.14.1", {"start": v(-55.44, -22.27) * mm, "end": v(-53.56, -23.35) * mm, "construction": true});
            skLineSegment(sketch, "E60.14.2", {"start": v(-53.56, -23.35) * mm, "end": v(-45.01, -6.83) * mm});
            skLineSegment(sketch, "E60.14.3", {"start": v(-50.5, -21.25) * mm, "end": v(-44.49, -7.07) * mm});
            skLineSegment(sketch, "E60.14.4", {"start": v(-48, -22.15) * mm, "end": v(-50.5, -21.25) * mm});
            skLineSegment(sketch, "E60.14.5", {"start": v(-48, -22.15) * mm, "end": v(-43.66, -7.37) * mm});
            skLineSegment(sketch, "E60.15.0", {"start": v(-43.1, -7.51) * mm, "end": v(-46.98, -25.7) * mm});
            skLineSegment(sketch, "E60.15.1", {"start": v(-46.98, -25.7) * mm, "end": v(-44.84, -26.07) * mm, "construction": true});
            skLineSegment(sketch, "E60.15.2", {"start": v(-44.84, -26.07) * mm, "end": v(-42.47, -7.62) * mm});
            skLineSegment(sketch, "E60.15.3", {"start": v(-42.7, -23.05) * mm, "end": v(-41.89, -7.67) * mm});
            skLineSegment(sketch, "E60.15.4", {"start": v(-40.04, -23.04) * mm, "end": v(-42.7, -23.05) * mm});
            skLineSegment(sketch, "E60.15.5", {"start": v(-40.04, -23.04) * mm, "end": v(-41, -7.67) * mm});
            skLineSegment(sketch, "E60.16.0", {"start": v(-40.43, -7.6) * mm, "end": v(-37.86, -26.03) * mm});
            skLineSegment(sketch, "E60.16.1", {"start": v(-37.86, -26.03) * mm, "end": v(-35.73, -25.64) * mm, "construction": true});
            skLineSegment(sketch, "E60.16.2", {"start": v(-35.73, -25.64) * mm, "end": v(-39.8, -7.5) * mm});
            skLineSegment(sketch, "E60.16.3", {"start": v(-34.74, -22.08) * mm, "end": v(-39.24, -7.35) * mm});
            skLineSegment(sketch, "E60.16.4", {"start": v(-32.24, -21.15) * mm, "end": v(-34.74, -22.08) * mm});
            skLineSegment(sketch, "E60.16.5", {"start": v(-32.24, -21.15) * mm, "end": v(-38.41, -7.04) * mm});
            skLineSegment(sketch, "E60.17.0", {"start": v(-37.89, -6.79) * mm, "end": v(-29.18, -23.22) * mm});
            skLineSegment(sketch, "E60.17.1", {"start": v(-29.18, -23.22) * mm, "end": v(-27.3, -22.13) * mm, "construction": true});
            skLineSegment(sketch, "E60.17.2", {"start": v(-27.3, -22.13) * mm, "end": v(-37.34, -6.47) * mm});
            skLineSegment(sketch, "E60.17.3", {"start": v(-27.6, -18.44) * mm, "end": v(-36.86, -6.14) * mm});
            skLineSegment(sketch, "E60.17.4", {"start": v(-25.57, -16.72) * mm, "end": v(-27.6, -18.44) * mm});
            skLineSegment(sketch, "E60.17.5", {"start": v(-25.57, -16.72) * mm, "end": v(-36.19, -5.56) * mm});
            skArc(sketch, "E61", {"start": v(-45.09, 6.79) * mm, "mid": v(-45.36, 6.63) * mm, "end": v(-45.63, 6.47) * mm});
            skArc(sketch, "E62.trimOffspring", {"start": v(-46.11, 6.14) * mm, "mid": v(-46.46, 5.86) * mm, "end": v(-46.79, 5.56) * mm});
            skArc(sketch, "E63.trimOffspring", {"start": v(-47.2, 5.15) * mm, "mid": v(-47.4, 4.9) * mm, "end": v(-47.6, 4.66) * mm});
            skArc(sketch, "E64.trimOffspring", {"start": v(-47.93, 4.18) * mm, "mid": v(-48.16, 3.8) * mm, "end": v(-48.37, 3.42) * mm});
            skArc(sketch, "E65.trimOffspring", {"start": v(-48.6, 2.89) * mm, "mid": v(-48.72, 2.6) * mm, "end": v(-48.82, 2.29) * mm});
            skArc(sketch, "E66.trimOffspring", {"start": v(-48.97, 1.73) * mm, "mid": v(-49.06, 1.3) * mm, "end": v(-49.12, 0.86) * mm});
            skArc(sketch, "E67.trimOffspring", {"start": v(-43.73, 7.35) * mm, "mid": v(-44.15, 7.2) * mm, "end": v(-44.56, 7.04) * mm});
            skArc(sketch, "E68.trimOffspring", {"start": v(-42.55, 7.6) * mm, "mid": v(-42.86, 7.56) * mm, "end": v(-43.17, 7.5) * mm});
            skArc(sketch, "E69.trimOffspring", {"start": v(-41.08, 7.67) * mm, "mid": v(-41.53, 7.68) * mm, "end": v(-41.97, 7.67) * mm});
            skArc(sketch, "E70.trimOffspring", {"start": v(-39.88, 7.51) * mm, "mid": v(-40.2, 7.57) * mm, "end": v(-40.5, 7.62) * mm});
            skArc(sketch, "E71.trimOffspring", {"start": v(-38.48, 7.07) * mm, "mid": v(-38.9, 7.23) * mm, "end": v(-39.32, 7.37) * mm});
            skArc(sketch, "E72.trimOffspring", {"start": v(-37.4, 6.51) * mm, "mid": v(-37.68, 6.67) * mm, "end": v(-37.96, 6.83) * mm});
            skArc(sketch, "E73.trimOffspring", {"start": v(-36.25, 5.62) * mm, "mid": v(-36.58, 5.91) * mm, "end": v(-36.93, 6.18) * mm});
            skArc(sketch, "E74.trimOffspring", {"start": v(-35.43, 4.72) * mm, "mid": v(-35.63, 4.97) * mm, "end": v(-35.84, 5.2) * mm});
            skArc(sketch, "E75.trimOffspring", {"start": v(-34.64, 3.49) * mm, "mid": v(-34.85, 3.88) * mm, "end": v(-35.09, 4.25) * mm});
            skArc(sketch, "E76.trimOffspring", {"start": v(-34.18, 2.37) * mm, "mid": v(-34.28, 2.67) * mm, "end": v(-34.4, 2.96) * mm});
            skArc(sketch, "E77.trimOffspring", {"start": v(-33.86, 0.94) * mm, "mid": v(-33.93, 1.37) * mm, "end": v(-34.02, 1.8) * mm});
            skArc(sketch, "E78.trimOffspring", {"start": v(-33.8, -0.28) * mm, "mid": v(-33.8, 0.04) * mm, "end": v(-33.81, 0.36) * mm});
            skArc(sketch, "E79.trimOffspring", {"start": v(-49.11, -0.94) * mm, "mid": v(-48.91, -1.97) * mm, "end": v(-48.58, -2.96) * mm});
            skArc(sketch, "E80.trimOffspring", {"start": v(-48.33, -3.49) * mm, "mid": v(-48.12, -3.88) * mm, "end": v(-47.89, -4.25) * mm});
            skArc(sketch, "E81.trimOffspring", {"start": v(-47.55, -4.72) * mm, "mid": v(-47.35, -4.97) * mm, "end": v(-47.14, -5.2) * mm});
            skArc(sketch, "E82.trimOffspring", {"start": v(-46.73, -5.62) * mm, "mid": v(-46.4, -5.91) * mm, "end": v(-46.05, -6.18) * mm});
            skArc(sketch, "E83.trimOffspring", {"start": v(-45.57, -6.51) * mm, "mid": v(-45.3, -6.67) * mm, "end": v(-45.01, -6.83) * mm});
            skArc(sketch, "E84.trimOffspring", {"start": v(-44.49, -7.07) * mm, "mid": v(-44.08, -7.23) * mm, "end": v(-43.66, -7.37) * mm});
            skArc(sketch, "E85.trimOffspring", {"start": v(-43.1, -7.51) * mm, "mid": v(-42.78, -7.57) * mm, "end": v(-42.47, -7.62) * mm});
            skArc(sketch, "E86.trimOffspring", {"start": v(-41.89, -7.67) * mm, "mid": v(-41.45, -7.68) * mm, "end": v(-41, -7.67) * mm});
            skArc(sketch, "E87.trimOffspring", {"start": v(-40.43, -7.6) * mm, "mid": v(-40.11, -7.56) * mm, "end": v(-39.8, -7.5) * mm});
            skArc(sketch, "E88.trimOffspring", {"start": v(-39.24, -7.35) * mm, "mid": v(-38.82, -7.2) * mm, "end": v(-38.41, -7.04) * mm});
            skArc(sketch, "E89.trimOffspring", {"start": v(-37.89, -6.79) * mm, "mid": v(-37.61, -6.63) * mm, "end": v(-37.34, -6.47) * mm});
            skArc(sketch, "E90.trimOffspring", {"start": v(-36.86, -6.14) * mm, "mid": v(-36.52, -5.86) * mm, "end": v(-36.19, -5.56) * mm});
            skArc(sketch, "E91.trimOffspring", {"start": v(-35.78, -5.15) * mm, "mid": v(-35.58, -4.9) * mm, "end": v(-35.38, -4.66) * mm});
            skArc(sketch, "E92.trimOffspring", {"start": v(-35.04, -4.18) * mm, "mid": v(-34.81, -3.8) * mm, "end": v(-34.6, -3.42) * mm});
            skArc(sketch, "E93.trimOffspring", {"start": v(-34.37, -2.89) * mm, "mid": v(-34.27, -2.64) * mm, "end": v(-34.18, -2.38) * mm});
            skLineSegment(sketch, "E94", {"start": v(-19.45, -6.88) * mm, "end": v(-34.18, -2.38) * mm});
            skArc(sketch, "E95.trimOffspring", {"start": v(-34, -1.73) * mm, "mid": v(-33.91, -1.3) * mm, "end": v(-33.85, -0.86) * mm});
            skLineSegment(sketch, "E96", {"start": v(-62.22, -16.16) * mm, "end": v(-60.81, -17.81) * mm});
            skLineSegment(sketch, "E97", {"start": v(-65.74, -10.13) * mm, "end": v(-66.5, -8.1) * mm});
            skLineSegment(sketch, "E98", {"start": v(-67.74, -1.22) * mm, "end": v(-67.75, 0.95) * mm});
            skLineSegment(sketch, "E99", {"start": v(-66.57, 7.83) * mm, "end": v(-65.84, 9.87) * mm});
            skLineSegment(sketch, "E100", {"start": v(-37.86, -26.03) * mm, "end": v(-35.73, -25.64) * mm});
            skLineSegment(sketch, "E101", {"start": v(-29.18, -23.22) * mm, "end": v(-27.3, -22.13) * mm});
            skLineSegment(sketch, "E102", {"start": v(-21.98, -17.6) * mm, "end": v(-20.6, -15.94) * mm});
            skLineSegment(sketch, "E103", {"start": v(-46.98, -25.7) * mm, "end": v(-44.84, -26.07) * mm});
            skLineSegment(sketch, "E104", {"start": v(-53.56, -23.35) * mm, "end": v(-55.44, -22.27) * mm});
            skLineSegment(sketch, "E105", {"start": v(-62.38, 15.94) * mm, "end": v(-61, 17.6) * mm});
            skLineSegment(sketch, "E106", {"start": v(-55.67, 22.13) * mm, "end": v(-53.8, 23.22) * mm});
            skLineSegment(sketch, "E107", {"start": v(-47.25, 25.64) * mm, "end": v(-45.11, 26.03) * mm});
            skLineSegment(sketch, "E108", {"start": v(-38.13, 26.07) * mm, "end": v(-36, 25.7) * mm});
            skLineSegment(sketch, "E109", {"start": v(-29.42, 23.35) * mm, "end": v(-27.53, 22.27) * mm});
            skLineSegment(sketch, "E110", {"start": v(-22.16, 17.81) * mm, "end": v(-20.76, 16.16) * mm});
            skLineSegment(sketch, "E111", {"start": v(-17.23, 10.13) * mm, "end": v(-16.48, 8.1) * mm});
            skLineSegment(sketch, "E112", {"start": v(-15.23, 1.22) * mm, "end": v(-15.22, -0.95) * mm});
            skLineSegment(sketch, "E113", {"start": v(-16.4, -7.83) * mm, "end": v(-17.13, -9.87) * mm});
            skLineSegment(sketch, "E114", {"start": v(-49.16, -0.36) * mm, "end": v(-49.17, 0.28) * mm});
            skSolve(sketch);
        }
        {
            var Q0;
            Q0=qSketchRegion(id+"F9",true);
            extrude(context, id + "F10", {"entities" : qUnion([Q0]), "operationType" : NewBodyOperationType.REMOVE, "depth" : 4.5 * mm});
        }
        {
            var Q0;
            Q0=makeQuery(id+"F0.imprint","IMPRINT",FACE,{"disambiguationData":[TD([[makeQuery(id+"F0.imprint","IMPRINT",EDGE,{"derivedFrom":sQuery(id+"F0.wireOp",EDGE,"E0")}),-1.0]])]});
            var sketch = newSketch(context, id + "F11", { "sketchPlane" : qUnion([Q0])});
            skCircle(sketch, "E115", {"center": v(-41.49, 0) * mm, "radius": 5.37 * mm});
            skCircle(sketch, "E116", {"center": v(-41.49, 0) * mm, "radius": 7.09 * mm});
            skLineSegment(sketch, "E117.bottom", {"start": v(-41.49, 0) * mm, "end": v(-41.49, 0) * mm});
            skSolve(sketch);
        }
        {
            var Q0;
            Q0=qSketchRegion(id+"F11",true);
            var Q1;
            Q1=makeQuery(id+"F10.boolean.opBoolean","COPY",FACE,{"derivedFrom":makeQuery(id+"F10.opExtrude","CAP_FACE",FACE,{"disambiguationData":[OSD([sQuery(id+"F9.wireOp",EDGE,"E60.11.3"),sQuery(id+"F9.wireOp",EDGE,"E60.11.4"),sQuery(id+"F9.wireOp",EDGE,"E60.11.5"),sQuery(id+"F9.wireOp",EDGE,"E79.trimOffspring")])],"isStart":false})});
            extrude(context, id + "F12", {"entities" : qUnion([Q0]), "operationType" : NewBodyOperationType.REMOVE, "endBound" : BoundingType.UP_TO_SURFACE, "endBoundEntityFace" : qUnion([Q1]), "depth" : 25 * mm});
        }
        {
            var Q0;
            {var subQ0=sQuery(id+"F0.wireOp",EDGE,"E36");var subQ1=sQuery(id+"F0.wireOp",EDGE,"E35");var subQ2=sQuery(id+"F0.wireOp",EDGE,"E34");var subQ3=sQuery(id+"F0.wireOp",EDGE,"E33");var subQ4=sQuery(id+"F0.wireOp",EDGE,"E32");var subQ5=sQuery(id+"F0.wireOp",EDGE,"E31");var subQ6=sQuery(id+"F0.wireOp",EDGE,"E30");var subQ7=sQuery(id+"F0.wireOp",EDGE,"E29");var subQ8=sQuery(id+"F0.wireOp",EDGE,"E28");var subQ9=sQuery(id+"F0.wireOp",EDGE,"E27");var subQ10=sQuery(id+"F0.wireOp",EDGE,"E26");var subQ11=sQuery(id+"F0.wireOp",EDGE,"E25");var subQ12=sQuery(id+"F0.wireOp",EDGE,"E24");var subQ13=sQuery(id+"F0.wireOp",EDGE,"E23");var subQ14=sQuery(id+"F0.wireOp",EDGE,"E22");var subQ15=sQuery(id+"F0.wireOp",EDGE,"E21");var subQ16=sQuery(id+"F0.wireOp",EDGE,"E20");var subQ17=sQuery(id+"F0.wireOp",EDGE,"E19");var subQ18=sQuery(id+"F0.wireOp",EDGE,"E18");var subQ19=sQuery(id+"F0.wireOp",EDGE,"E17");var subQ20=sQuery(id+"F0.wireOp",EDGE,"E16");var subQ21=sQuery(id+"F0.wireOp",EDGE,"E15");var subQ22=sQuery(id+"F0.wireOp",EDGE,"E14");var subQ23=sQuery(id+"F0.wireOp",EDGE,"E13");var subQ24=sQuery(id+"F0.wireOp",EDGE,"E12");var subQ25=sQuery(id+"F0.wireOp",EDGE,"E11");var subQ26=sQuery(id+"F0.wireOp",EDGE,"E10");var subQ27=sQuery(id+"F0.wireOp",EDGE,"E9");var subQ28=sQuery(id+"F0.wireOp",EDGE,"E8");var subQ29=sQuery(id+"F0.wireOp",EDGE,"E7");var subQ30=sQuery(id+"F0.wireOp",EDGE,"E6");var subQ31=sQuery(id+"F0.wireOp",EDGE,"E5");var subQ32=sQuery(id+"F0.wireOp",EDGE,"E4");var subQ33=sQuery(id+"F0.wireOp",EDGE,"E3");var subQ34=sQuery(id+"F0.wireOp",EDGE,"E1");var subQ35=sQuery(id+"F0.wireOp",EDGE,"E0");Q0=makeQuery(id+"F5.boolean.opBoolean","MERGE",FACE,{"derivedFrom":[makeQuery(id+"F1.opExtrude","CAP_FACE",FACE,{"disambiguationData":[OSD([subQ35,subQ34,subQ33,subQ32,subQ31,subQ30,subQ29,subQ28,subQ27,subQ26,subQ25,subQ24,subQ23,subQ22,subQ21,subQ20,subQ19,subQ18,subQ17,subQ16,subQ15,subQ14,subQ13,subQ12,subQ11,subQ10,subQ9,subQ8,subQ7,subQ6,subQ5,subQ4,subQ3,subQ2,subQ1,subQ0])],"isStart":false}),makeQuery(id+"F5.opExtrude","CAP_FACE",FACE,{"disambiguationData":[OSD([subQ35,subQ34,subQ33,subQ32,subQ31,subQ30,subQ29,subQ28,subQ27,subQ26,subQ25,subQ24,subQ23,subQ22,subQ21,subQ20,subQ19,subQ18,subQ17,subQ16,subQ15,subQ14,subQ13,subQ12,subQ11,subQ10,subQ9,subQ8,subQ7,subQ6,subQ5,subQ4,subQ3,subQ2,subQ1,subQ0])],"isStart":false})]});}
            var sketch = newSketch(context, id + "F13", { "sketchPlane" : qUnion([Q0])});
            skText(sketch, "E118", { "text": "    Ian\nAguirre", "fontName": "OpenSans-Bold.ttf"});
            const initialGuessF13  = {"E118": [-0.06245, 0.00587, 1, 0, 0.00823]};
            skSetInitialGuess(sketch, initialGuessF13);
            skSolve(sketch);
        }
        {
            var Q0;
            Q0=qSketchRegion(id+"F13",true);
            extrude(context, id + "F14", {"entities" : qUnion([Q0]), "operationType" : NewBodyOperationType.ADD, "depth" : 3 * mm});
        }
    });
